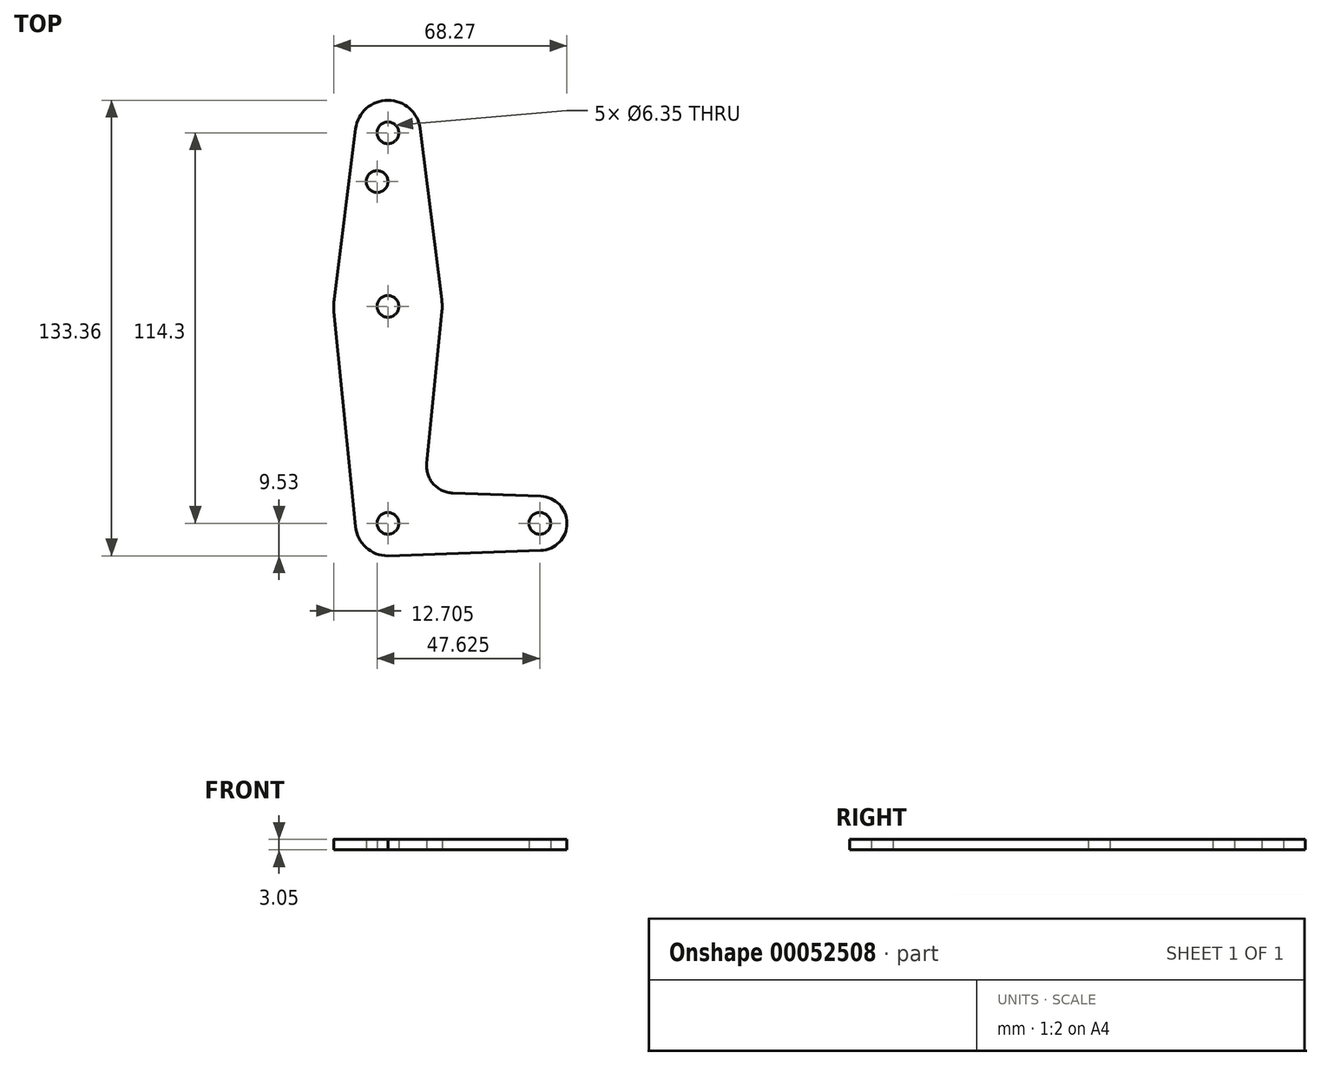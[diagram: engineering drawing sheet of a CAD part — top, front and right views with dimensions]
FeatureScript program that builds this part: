
annotation { "Feature Type Name" : "Feature", "Feature Type Description" : "" }
export const myFeature = defineFeature(function(context is Context, id is Id, definition is map)
    precondition{}
    {
        {
            var Q0;
            Q0=qCreatedBy(makeId("Top.planeOp"),FACE);
            var sketch = newSketch(context, id + "F0", { "sketchPlane" : qUnion([Q0])});
            skCircle(sketch, "E0", {"center": v(0, 0) * mm, "radius": 9.53 * mm});
            skLineSegment(sketch, "E1", {"start": v(0, 0) * mm, "end": v(0, 114.3) * mm, "construction": true});
            skLineSegment(sketch, "E2", {"start": v(0, 0) * mm, "end": v(44.45, 0) * mm, "construction": true});
            skCircle(sketch, "E3", {"center": v(0, 114.3) * mm, "radius": 9.53 * mm});
            skCircle(sketch, "E4", {"center": v(44.45, 0) * mm, "radius": 7.94 * mm});
            skCircle(sketch, "E5", {"center": v(0, 63.5) * mm, "radius": 15.88 * mm});
            skLineSegment(sketch, "E6", {"start": v(-9.45, 115.5) * mm, "end": v(-15.75, 65.48) * mm});
            skLineSegment(sketch, "E7", {"start": v(9.45, 115.5) * mm, "end": v(15.75, 65.48) * mm});
            skLineSegment(sketch, "E8", {"start": v(0, -9.53) * mm, "end": v(44.73, -7.93) * mm});
            skLineSegment(sketch, "E9", {"start": v(18.97, 8.85) * mm, "end": v(44.73, 7.93) * mm});
            skLineSegment(sketch, "E10", {"start": v(-15.8, 61.91) * mm, "end": v(-9.48, -0.95) * mm});
            skLineSegment(sketch, "E11", {"start": v(15.8, 61.91) * mm, "end": v(11.34, 17.6) * mm});
            skArc(sketch, "E12.filletArc", {"start": v(11.34, 17.6) * mm, "mid": v(13.26, 11.57) * mm, "end": v(18.97, 8.85) * mm});
            skCircle(sketch, "E13", {"center": v(0, 114.3) * mm, "radius": 3.18 * mm});
            skCircle(sketch, "E14", {"center": v(0, 63.5) * mm, "radius": 3.18 * mm});
            skCircle(sketch, "E15", {"center": v(0, 0) * mm, "radius": 3.18 * mm});
            skCircle(sketch, "E16", {"center": v(44.45, 0) * mm, "radius": 3.18 * mm});
            skCircle(sketch, "E17", {"center": v(-3.18, 100.03) * mm, "radius": 3.18 * mm});
            skLineSegment(sketch, "E18", {"start": v(-3.18, 100.03) * mm, "end": v(0, 100.03) * mm, "construction": true});
            skSolve(sketch);
        }
        {
            var Q0;
            Q0=makeQuery(id+"F0.imprint","IMPRINT",FACE,{"disambiguationData":[TD([[makeQuery(id+"F0.imprint","IMPRINT",EDGE,{"derivedFrom":sQuery(id+"F0.wireOp",EDGE,"E13")}),-1.0]])]});
            var Q1;
            {var subQ1=sQuery(id+"F0.wireOp",EDGE,"E6");Q1=makeQuery(id+"F0.imprint","IMPRINT",FACE,{"disambiguationData":[TD([[makeQuery(id+"F0.imprint","IMPRINT",EDGE,{"derivedFrom":subQ1}),1.0]])]});}
            var Q2;
            Q2=makeQuery(id+"F0.imprint","IMPRINT",FACE,{"disambiguationData":[TD([[makeQuery(id+"F0.imprint","IMPRINT",EDGE,{"derivedFrom":sQuery(id+"F0.wireOp",EDGE,"E14")}),-1.0]])]});
            var Q3;
            {var subQ8=sQuery(id+"F0.wireOp",EDGE,"E9");Q3=makeQuery(id+"F0.imprint","IMPRINT",FACE,{"disambiguationData":[TD([[makeQuery(id+"F0.imprint","IMPRINT",EDGE,{"derivedFrom":subQ8}),-1.0]])]});}
            var Q4;
            Q4=makeQuery(id+"F0.imprint","IMPRINT",FACE,{"disambiguationData":[TD([[makeQuery(id+"F0.imprint","IMPRINT",EDGE,{"derivedFrom":sQuery(id+"F0.wireOp",EDGE,"E15")}),-1.0]])]});
            var Q5;
            Q5=makeQuery(id+"F0.imprint","IMPRINT",FACE,{"disambiguationData":[TD([[makeQuery(id+"F0.imprint","IMPRINT",EDGE,{"derivedFrom":sQuery(id+"F0.wireOp",EDGE,"E16")}),-1.0]])]});
            extrude(context, id + "F1", {"entities" : qUnion([Q0, Q1, Q2, Q3, Q4, Q5]), "depth" : 3.05 * mm});
        }
    });
